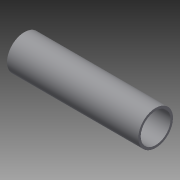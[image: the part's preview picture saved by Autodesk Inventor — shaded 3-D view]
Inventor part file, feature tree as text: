
AUTODESK INVENTOR PART (.ipt)
format: ipt  version: 2015 SP1 (Build 190203100, 203)  size: 76,800 bytes
history: native  units: in
note: dims shown in document units (in); Inventor stores cm internally (conversion verified against a paired STEP export)
features: extrude x1, sketch x1
ambient origin geometry x8: Origin, YZ Plane, XZ Plane, XY Plane, X Axis, Y Axis, Z Axis, Center Point
bodies: Solid1 (feature_tree)
feature tree (2):
  extrude  "Extrusion1"  Depth=8.875in
  sketch  "Sketch1"  dims[d0=2.047in d1=2.375in d2=8.875in d3=0.0in]
